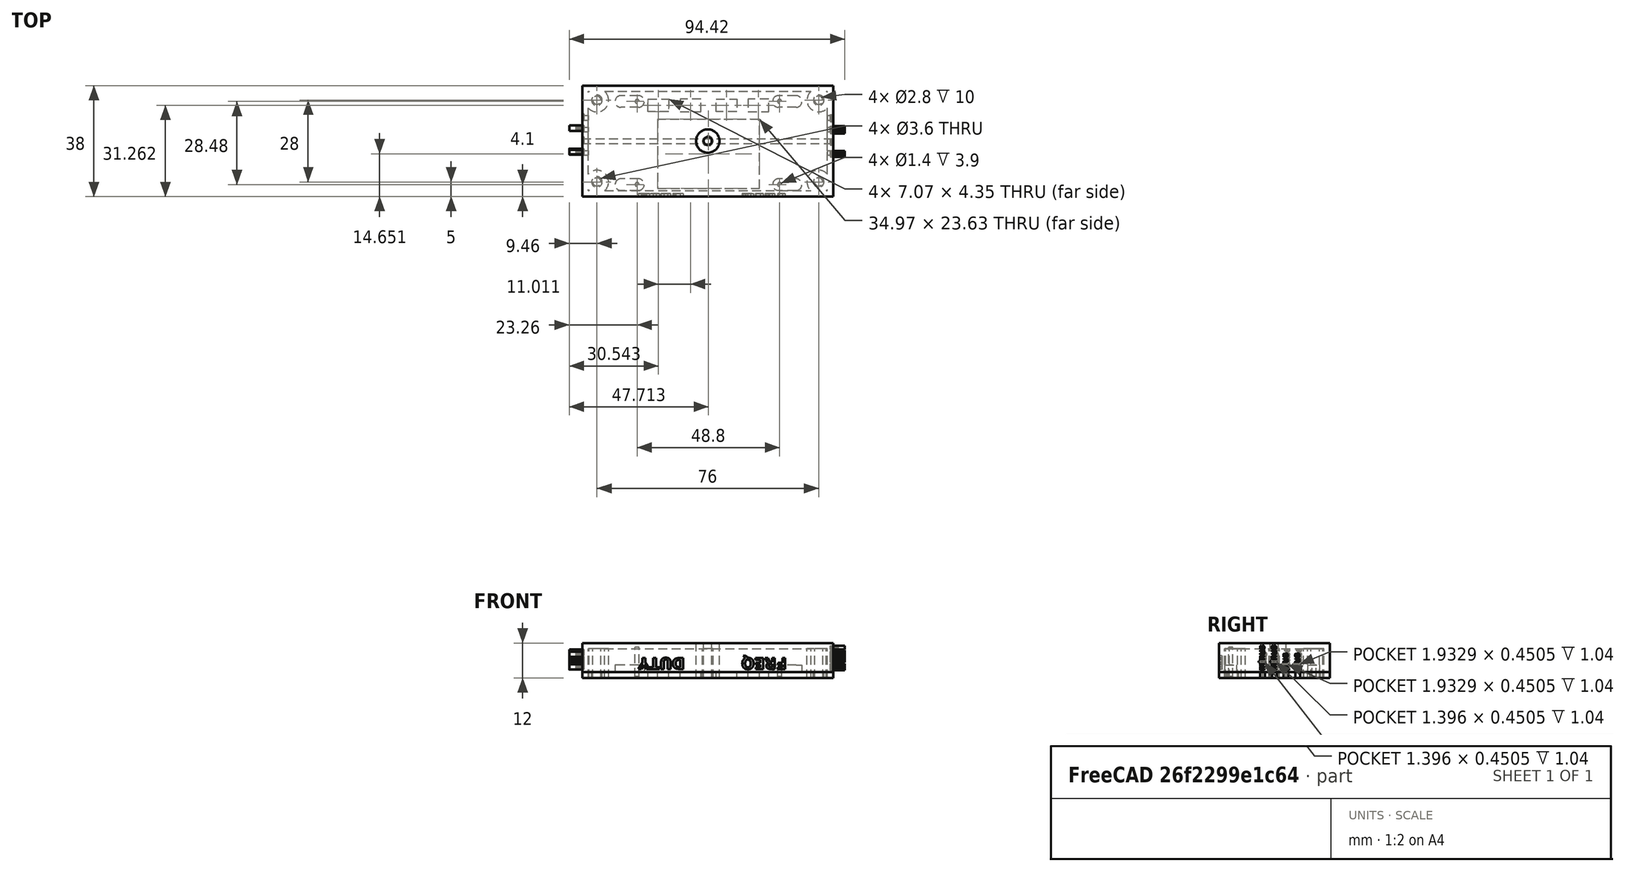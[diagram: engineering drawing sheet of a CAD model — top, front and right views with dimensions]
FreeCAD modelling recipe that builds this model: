
FCSTD DOCUMENT  (FreeCAD 0.19R)
Label: lpwm_v2
License: All rights reserved
LicenseURL: http://en.wikipedia.org/wiki/All_rights_reserved
objects: Part::FeaturePython×10, Part::Part2DObjectPython×7, PartDesign::Body×7, Part::Extrusion×6, PartDesign::FeatureBase×6, Part::Cylinder×4, Part::MultiFuse×4, Part::Cut×3, Part::Box×3, Sketcher::SketchObject×2, PartDesign::Pad×2, App::Part×2, Mesh::Feature×1, Part::Feature×1, Part::Refine×1
note: 48 computed .brp shape members not serialized (recipe doc carries the construction recipe); baked Part::Feature solids carry a one-line shape summary decoded from their .brp

FEATURE [Mesh::Feature] LPWM_pwmGenerator_cover  label="LPWM_pwmGenerator-cover"
FEATURE [Part::Feature] LPWM_pwmGenerator_cover001
  shape: bbox 56.46 x 36.68 x 3.899 mm, 1714 faces, 0 solids (baked)
FEATURE [Part::Refine] LPWM_pwmGenerator_cover001001
  Source = -> LPWM_pwmGenerator_cover001
FEATURE [Part::Part2DObjectPython] Shape2DView  # Draft 2D object (typed FeaturePython)
  Base = -> LPWM_pwmGenerator_cover001001
  FuseArch = false
  HiddenLines = false
  InPlace = true
  Projection = (0.00719287,0.00574245,0.999958)
  ProjectionMode = 0
  SegmentLength = 0.05
  Tessellation = false
  VisibleOnly = false
FEATURE [Sketcher::SketchObject] Sketch  label="top plate sketch"
  ExternalGeometry = -> [Shape2DView]
  FullyConstrained = true
  MapMode = 5
  sketch-geometry (24):
    g0: LineSegment StartX=-20.4532 StartY=14.4374 StartZ=0 EndX=-13.3806 EndY=14.4374 EndZ=0
    g1: LineSegment StartX=-13.3806 StartY=14.4374 StartZ=0 EndX=-13.3806 EndY=10.0869 EndZ=0
    g2: LineSegment StartX=-13.3806 StartY=10.0869 StartZ=0 EndX=-20.4532 EndY=10.0869 EndZ=0
    g3: LineSegment StartX=-20.4532 StartY=10.0869 StartZ=0 EndX=-20.4532 EndY=14.4374 EndZ=0
    g4: LineSegment StartX=-9.44208 StartY=10.0867 StartZ=0 EndX=-2.36949 EndY=10.0867 EndZ=0
    g5: LineSegment StartX=-2.36949 StartY=10.0867 StartZ=0 EndX=-2.36949 EndY=14.4366 EndZ=0
    g6: LineSegment StartX=-2.36949 StartY=14.4366 StartZ=0 EndX=-9.44208 EndY=14.4366 EndZ=0
    g7: LineSegment StartX=-9.44208 StartY=14.4366 StartZ=0 EndX=-9.44208 EndY=10.0867 EndZ=0
    g8: LineSegment StartX=2.84142 StartY=14.4364 StartZ=0 EndX=9.91401 EndY=14.4364 EndZ=0
    g9: LineSegment StartX=9.91401 StartY=14.4364 StartZ=0 EndX=9.91401 EndY=10.0859 EndZ=0
    g10: LineSegment StartX=9.91401 StartY=10.0859 StartZ=0 EndX=2.84142 EndY=10.0859 EndZ=0
    g11: LineSegment StartX=2.84142 StartY=10.0859 StartZ=0 EndX=2.84142 EndY=14.4364 EndZ=0
    g12: LineSegment StartX=13.7837 StartY=10.0858 StartZ=0 EndX=20.8563 EndY=10.0858 EndZ=0
    g13: LineSegment StartX=20.8563 StartY=10.0858 StartZ=0 EndX=20.8563 EndY=14.4357 EndZ=0
    g14: LineSegment StartX=20.8563 StartY=14.4357 StartZ=0 EndX=13.7837 EndY=14.4357 EndZ=0
    g15: LineSegment StartX=13.7837 StartY=14.4357 StartZ=0 EndX=13.7837 EndY=10.0858 EndZ=0
    g16: LineSegment StartX=17.7369 StartY=7.46801 StartZ=0 EndX=-17.2306 EndY=7.46801 EndZ=0
    g17: LineSegment StartX=-17.2306 StartY=7.46801 StartZ=0 EndX=-17.2306 EndY=-16.1666 EndZ=0
    g18: LineSegment StartX=-17.2306 StartY=-16.1666 StartZ=0 EndX=17.7369 EndY=-16.1666 EndZ=0
    g19: LineSegment StartX=17.7369 StartY=-16.1666 StartZ=0 EndX=17.7369 EndY=7.46801 EndZ=0
    g20: LineSegment StartX=-43 StartY=19 StartZ=0 EndX=43 EndY=19 EndZ=0
    g21: LineSegment StartX=43 StartY=19 StartZ=0 EndX=43 EndY=-19 EndZ=0
    g22: LineSegment StartX=43 StartY=-19 StartZ=0 EndX=-43 EndY=-19 EndZ=0
    g23: LineSegment StartX=-43 StartY=-19 StartZ=0 EndX=-43 EndY=19 EndZ=0
  constraints (60):
    c: Coincident(g0,g1)
    c: Coincident(g1,g2)
    c: Coincident(g2,g3)
    c: Coincident(g3,g0)
    c: Horizontal(g0)
    c: Horizontal(g2)
    c: Vertical(g1)
    c: Vertical(g3)
    c: Coincident(g0,g-5)
    c: Coincident(g1,g-6)
    c: Coincident(g4,g5)
    c: Coincident(g5,g6)
    c: Coincident(g6,g7)
    c: Coincident(g7,g4)
    c: Horizontal(g4)
    c: Horizontal(g6)
    c: Vertical(g5)
    c: Vertical(g7)
    c: Coincident(g4,g-7)
    c: Coincident(g5,g-9)
    c: Coincident(g8,g9)
    c: Coincident(g9,g10)
    c: Coincident(g10,g11)
    c: Coincident(g11,g8)
    c: Horizontal(g8)
    c: Horizontal(g10)
    c: Vertical(g9)
    c: Vertical(g11)
    c: Coincident(g8,g-12)
    c: Coincident(g9,g-14)
    c: Coincident(g12,g13)
    c: Coincident(g13,g14)
    c: Coincident(g14,g15)
    c: Coincident(g15,g12)
    c: Horizontal(g12)
    c: Horizontal(g14)
    c: Vertical(g13)
    c: Vertical(g15)
    c: Coincident(g12,g-15)
    c: Coincident(g13,g-17)
    c: Coincident(g16,g17)
    c: Coincident(g17,g18)
    c: Coincident(g18,g19)
    c: Coincident(g19,g16)
    c: Horizontal(g16)
    c: Horizontal(g18)
    c: Vertical(g17)
    c: Vertical(g19)
    c: Coincident(g16,g-22)
    c: Coincident(g17,g-20)
    c: Coincident(g20,g21)
    c: Coincident(g21,g22)
    c: Coincident(g22,g23)
    c: Coincident(g23,g20)
    c: Horizontal(g20)
    c: Vertical(g21)
    c: DistanceX(g20,g20) = 86
    c: Symmetric(g22,g21,g-2)
    c: DistanceY(g23,g23) = 38
    c: Symmetric(g20,g22,g-1)
FEATURE [PartDesign::Pad] Pad  label="top plate body"
  Direction = (1,1,1)
  Length = 2
  Length2 = 100
  Profile = -> Sketch
  Type = 0
FEATURE [Part::Cylinder] Cylinder  label="screw hole"
  Angle = 360
  AttacherType = Attacher::AttachEngine3D
  Height = 10
  Placement = pos=(-24.2,-14.9,0.5) rot=(0,0,1;0rad)
  Radius = 0.7
FEATURE [Part::FeaturePython] Array  label="screw hole array"  # Draft array (typed FeaturePython)
  Angle = 360
  ArrayType = 0
  Axis = (0,0,1)
  Base = -> Cylinder
  Center = (0,0,0)
  Count = 4
  ExpandArray = false
  Fuse = false
  IntervalAxis = (0,0,0)
  IntervalX = (48.8,0,0)
  IntervalY = (0,28.48,0)
  IntervalZ = (0,0,100)
  NumberCircles = 3
  NumberPolar = 5
  NumberX = 2
  NumberY = 2
  NumberZ = 1
  PlacementList = 4 placements: [(-24.2,-14.9,0.5),(-24.2,13.58,0.5),(24.6,-14.9,0.5),(24.6,13.58,0.5)]
  RadialDistance = 50
  ScaleList = (4) [(1,1,1),(1,1,1),(1,1,1),(1,1,1)]
  Symmetry = 1
  TangentialDistance = 25
FEATURE [Sketcher::SketchObject] Sketch001  label="screw hole stand sketch"
  AttachmentOffset = pos=(0,0,2) rot=(0,0,1;0rad)
  ExternalGeometry = -> [Shape2DView]
  FullyConstrained = false
  MapMode = 5
  Placement = pos=(0,0,2) rot=(0,0,1;0rad)
  sketch-geometry (4):
    g0: LineSegment StartX=-23.7668 StartY=-12.9169 StartZ=0 EndX=-29.7668 EndY=-12.9169 EndZ=0
    g1: LineSegment StartX=-23.7668 StartY=-16.9169 StartZ=0 EndX=-29.7668 EndY=-16.9169 EndZ=0
    g2: ArcOfCircle CenterX=-23.7668 CenterY=-14.9169 CenterZ=0 NormalX=0 NormalY=0 NormalZ=1 AngleXU=0 Radius=2 StartAngle=4.71239 EndAngle=7.85398
    g3: ArcOfCircle CenterX=-29.7668 CenterY=-14.9169 CenterZ=0 NormalX=0 NormalY=0 NormalZ=1 AngleXU=0 Radius=2 StartAngle=1.5708 EndAngle=4.71239
  constraints (9):
    c: Horizontal(g0)
    c: Horizontal(g1)
    c: DistanceY(g-3,g1) = 2
    c: DistanceY(g1,g0) = 4
    c: DistanceX(g0,g0) = 6
    c: Tangent(g2,g0) = -1.5708
    c: Tangent(g2,g1) = 1.5708
    c: Tangent(g3,g0) = -1.5708
    c: Tangent(g3,g1) = 1.5708
FEATURE [PartDesign::Pad] Pad001
  Direction = (1,1,1)
  Length = 2.4
  Length2 = 100
  Placement = pos=(0,0,2) rot=(0,0,1;0rad)
  Profile = -> Sketch001
  Type = 0
FEATURE [PartDesign::Body] Body
  Group = -> [Sketch001,Pad001]
  Origin = -> Origin
  Tip = -> Pad001
FEATURE [Part::FeaturePython] Array001  label="screw hole stand array"  # Draft array (typed FeaturePython)
  Angle = 360
  ArrayType = 0
  Axis = (0,0,1)
  Base = -> Body
  Center = (0,0,0)
  Count = 4
  ExpandArray = false
  Fuse = false
  IntervalAxis = (0,0,0)
  IntervalX = (54,0,0)
  IntervalY = (0,28.48,0)
  IntervalZ = (0,0,100)
  NumberCircles = 3
  NumberPolar = 5
  NumberX = 2
  NumberY = 2
  NumberZ = 1
  PlacementList = 4 placements: [(0,0,0),(0,28.48,0),(54,0,0),(54,28.48,0)]
  RadialDistance = 50
  ScaleList = (4) [(1,1,1),(1,1,1),(1,1,1),(1,1,1)]
  Symmetry = 1
  TangentialDistance = 25
FEATURE [Part::MultiFuse] Fusion  label="top plate fusion"
  Shapes = -> [Array001,Pad]
FEATURE [Part::Cylinder] Cylinder001  label="m3 bolt hole"
  Angle = 360
  AttacherType = Attacher::AttachEngine3D
  Height = 10
  Radius = 1.8
FEATURE [Part::FeaturePython] Array002  label="m3 bolt hole array"  # Draft array (typed FeaturePython)
  Angle = 360
  ArrayType = 0
  Axis = (0,0,1)
  Base = -> Cylinder001
  Center = (0,0,0)
  Count = 4
  ExpandArray = false
  Fuse = false
  IntervalAxis = (0,0,0)
  IntervalX = (76,0,0)
  IntervalY = (0,28,0)
  IntervalZ = (0,0,100)
  NumberCircles = 3
  NumberPolar = 5
  NumberX = 2
  NumberY = 2
  NumberZ = 1
  Placement = pos=(-38,-14,-2) rot=(0,0,1;0rad)
  PlacementList = 4 placements: [(0,0,0),(0,28,0),(76,0,0),(76,28,0)]
  RadialDistance = 50
  ScaleList = (4) [(1,1,1),(1,1,1),(1,1,1),(1,1,1)]
  Symmetry = 1
  TangentialDistance = 25
FEATURE [Part::MultiFuse] Fusion001  label="extract fusion"
  Shapes = -> [Array002,Array]
FEATURE [Part::Cut] Cut  label="top plate cut"
  Base = -> Fusion
  Tool = -> Fusion001
FEATURE [App::Part] Part  label="top plate part"
  Group = -> [Cut]
  Origin = -> Origin001
FEATURE [Part::Box] Box  label="bottom outer cube"
  AttacherType = Attacher::AttachEngine3D
  Height = 12
  Length = 86
  Placement = pos=(-43,-19,0) rot=(0,0,1;0rad)
  Width = 38
  expr: .Placement.Base.x = -Length / 2
  expr: .Placement.Base.y = -Width / 2
FEATURE [Part::Box] Box001  label="bottom extract cube"
  AttacherType = Attacher::AttachEngine3D
  Height = 10
  Length = 82
  Placement = pos=(-41,-17,0) rot=(0,0,1;0rad)
  Width = 34
  expr: .Placement.Base.y = -Width / 2
  expr: .Placement.Base.x = -Length / 2
FEATURE [Part::Cylinder] Cylinder002  label="for m3 bolt hole"
  Angle = 360
  AttacherType = Attacher::AttachEngine3D
  Height = 12
  Radius = 1.4
  expr: Height = <<bottom outer cube>>.Height
FEATURE [Part::FeaturePython] Array003  label="for m3 bolt hole array"  # Draft array (typed FeaturePython)
  Angle = 360
  ArrayType = 0
  Axis = (0,0,1)
  Base = -> Cylinder002
  Center = (0,0,0)
  Count = 4
  ExpandArray = false
  Fuse = false
  IntervalAxis = (0,0,0)
  IntervalX = (76,0,0)
  IntervalY = (0,28,0)
  IntervalZ = (0,0,100)
  NumberCircles = 3
  NumberPolar = 5
  NumberX = 2
  NumberY = 2
  NumberZ = 1
  Placement = pos=(-38,-14,-2) rot=(0,0,1;0rad)
  PlacementList = 4 placements: [(0,0,0),(0,28,0),(76,0,0),(76,28,0)]
  RadialDistance = 50
  ScaleList = (4) [(1,1,1),(1,1,1),(1,1,1),(1,1,1)]
  Symmetry = 1
  TangentialDistance = 25
FEATURE [Part::Cylinder] Cylinder003  label="for m3 bolt stand"
  Angle = 360
  AttacherType = Attacher::AttachEngine3D
  Height = 12
  Radius = 4
  expr: Height = <<bottom outer cube>>.Height
FEATURE [Part::FeaturePython] Array004  label="for m3 bolt stand array"  # Draft array (typed FeaturePython)
  Angle = 360
  ArrayType = 0
  Axis = (0,0,1)
  Base = -> Cylinder003
  Center = (0,0,0)
  Count = 4
  ExpandArray = false
  Fuse = false
  IntervalAxis = (0,0,0)
  IntervalX = (76,0,0)
  IntervalY = (0,28,0)
  IntervalZ = (0,0,100)
  NumberCircles = 3
  NumberPolar = 5
  NumberX = 2
  NumberY = 2
  NumberZ = 1
  Placement = pos=(-38,-14,0) rot=(0,0,1;0rad)
  PlacementList = 4 placements: [(0,0,0),(0,28,0),(76,0,0),(76,28,0)]
  RadialDistance = 50
  ScaleList = (4) [(1,1,1),(1,1,1),(1,1,1),(1,1,1)]
  Symmetry = 1
  TangentialDistance = 25
FEATURE [Part::Cut] Cut002  label="bottom cube cut"
  Base = -> Box
  Tool = -> Box001
FEATURE [Part::MultiFuse] Fusion002  label="bottom body fusion"
  Shapes = -> [Array004,Cut002]
FEATURE [Part::Box] Box002  label="wire hole"
  AttacherType = Attacher::AttachEngine3D
  Height = 2
  Length = 86
  Placement = pos=(-43,-0.8,0) rot=(0,0,1;0rad)
  Width = 1.6
  expr: Length = <<bottom outer cube>>.Length
  expr: .Placement.Base.y = -Width / 2
  expr: .Placement.Base.x = -Length / 2
FEATURE [Part::FeaturePython] Array005  label="wire hole array"  # Draft array (typed FeaturePython)
  Angle = 360
  ArrayType = 0
  Axis = (0,0,1)
  Base = -> Box002
  Center = (0,0,0)
  Count = 4
  ExpandArray = false
  Fuse = false
  IntervalAxis = (0,0,0)
  IntervalX = (100,0,0)
  IntervalY = (0,4,0)
  IntervalZ = (0,0,100)
  NumberCircles = 3
  NumberPolar = 5
  NumberX = 1
  NumberY = 4
  NumberZ = 1
  Placement = pos=(0,-4,0) rot=(0,0,1;0rad)
  PlacementList = 4 placements: arithmetic series from (-43,-0.8,0) step (0,4,0) to (-43,11.2,0)
  RadialDistance = 50
  ScaleList = (4) [(1,1,1),(1,1,1),(1,1,1),(1,1,1)]
  Symmetry = 1
  TangentialDistance = 25
  expr: .Placement.Base.y = -.IntervalY.y
FEATURE [Part::Part2DObjectPython] ShapeString  label="PWM ShapeString"  # Draft 2D object (typed FeaturePython)
  FontFile = <path>
  Placement = pos=(-37,-28.06,5.46) rot=(0,0,1;0rad)
  Size = 2
  String = PWM
  Tracking = 0
FEATURE [Part::Extrusion] Extrude
  Base = -> ShapeString
  Dir = (0,0,1)
  DirMode = 2
  FaceMakerClass = Part::FaceMakerBullseye
  LengthFwd = 5
  LengthRev = 0
  Solid = false
  Symmetric = false
FEATURE [PartDesign::FeatureBase] Clone
  BaseFeature = -> Extrude
FEATURE [PartDesign::Body] Body001  label="PWM text body"
  BaseFeature = -> Extrude
  Group = -> [Clone]
  Origin = -> Origin003
  Placement = pos=(-37,31.5,39.8) rot=(0,-1,0;1.5708rad)
  Tip = -> Clone
FEATURE [Part::FeaturePython] Array006  label="PWM text body array"  # Draft array (typed FeaturePython)
  Angle = 360
  ArrayType = 0
  Axis = (0,0,1)
  Base = -> Body001
  Center = (0,0,0)
  Count = 2
  ExpandArray = false
  Fuse = false
  IntervalAxis = (0,0,0)
  IntervalX = (100,0,0)
  IntervalY = (0,4,0)
  IntervalZ = (0,0,100)
  NumberCircles = 3
  NumberPolar = 5
  NumberX = 1
  NumberY = 2
  NumberZ = 1
  PlacementList = 2 placements: [(-37,31.5,39.8),(-37,35.5,39.8)]
  RadialDistance = 50
  ScaleList = (2) [(1,1,1),(1,1,1)]
  Symmetry = 1
  TangentialDistance = 25
FEATURE [Part::Part2DObjectPython] ShapeString001  label="GND ShapeString"  # Draft 2D object (typed FeaturePython)
  FontFile = <path>
  Placement = pos=(-37,-28.06,5.46) rot=(0,0,1;0rad)
  Size = 2
  String = GND
  Tracking = 0
FEATURE [Part::Extrusion] Extrude001
  Base = -> ShapeString001
  Dir = (0,0,1)
  DirMode = 2
  FaceMakerClass = Part::FaceMakerBullseye
  LengthFwd = 5
  LengthRev = 0
  Solid = false
  Symmetric = false
FEATURE [PartDesign::FeatureBase] Clone001
  BaseFeature = -> Extrude001
FEATURE [PartDesign::Body] Body002  label="GND text body"
  Group = -> [Clone001]
  Origin = -> Origin004
  Placement = pos=(-37,23.5,39.8) rot=(0,-1,0;1.5708rad)
  Tip = -> Clone001
FEATURE [Part::FeaturePython] Array007  label="GND text body array"  # Draft array (typed FeaturePython)
  Angle = 360
  ArrayType = 0
  Axis = (0,0,1)
  Base = -> Body002
  Center = (0,0,0)
  Count = 2
  ExpandArray = false
  Fuse = false
  IntervalAxis = (0,0,0)
  IntervalX = (100,0,0)
  IntervalY = (0,4,0)
  IntervalZ = (0,0,100)
  NumberCircles = 3
  NumberPolar = 5
  NumberX = 1
  NumberY = 2
  NumberZ = 1
  PlacementList = 2 placements: [(-37,23.5,39.8),(-37,27.5,39.8)]
  RadialDistance = 50
  ScaleList = (2) [(1,1,1),(1,1,1)]
  Symmetry = 1
  TangentialDistance = 25
FEATURE [Part::Part2DObjectPython] ShapeString002  label="MINUS ShapeString"  # Draft 2D object (typed FeaturePython)
  FontFile = <path>
  Placement = pos=(-37,-28.06,5.46) rot=(0,0,1;0rad)
  Size = 2
  String = minus
  Tracking = 0
FEATURE [Part::Extrusion] Extrude002
  Base = -> ShapeString002
  Dir = (0,0,1)
  DirMode = 2
  FaceMakerClass = Part::FaceMakerBullseye
  LengthFwd = 5
  LengthRev = 0
  Solid = false
  Symmetric = false
FEATURE [PartDesign::FeatureBase] Clone002
  BaseFeature = -> Extrude002
FEATURE [PartDesign::Body] Body003  label="MINUS text body"
  Group = -> [Clone002]
  Origin = -> Origin005
  Placement = pos=(36.5,-31.5,39.5) rot=(0.707107,0,0.707107;3.14159rad)
  Tip = -> Clone002
FEATURE [Part::FeaturePython] Array008  label="MINUS text body array"  # Draft array (typed FeaturePython)
  Angle = 360
  ArrayType = 0
  Axis = (0,0,1)
  Base = -> Body003
  Center = (0,0,0)
  Count = 2
  ExpandArray = false
  Fuse = false
  IntervalAxis = (0,0,0)
  IntervalX = (100,0,0)
  IntervalY = (0,4,0)
  IntervalZ = (0,0,100)
  NumberCircles = 3
  NumberPolar = 5
  NumberX = 1
  NumberY = 2
  NumberZ = 1
  PlacementList = 2 placements: [(36.5,-31.5,39.5),(36.5,-27.5,39.5)]
  RadialDistance = 50
  ScaleList = (2) [(1,1,1),(1,1,1)]
  Symmetry = 1
  TangentialDistance = 25
FEATURE [Part::Part2DObjectPython] ShapeString003  label="PLUS ShapeString001"  # Draft 2D object (typed FeaturePython)
  FontFile = <path>
  Placement = pos=(-37,-28.06,5.46) rot=(0,0,1;0rad)
  Size = 2
  String = plus
  Tracking = 0
FEATURE [Part::Extrusion] Extrude003
  Base = -> ShapeString003
  Dir = (0,0,1)
  DirMode = 2
  FaceMakerClass = Part::FaceMakerBullseye
  LengthFwd = 5
  LengthRev = 0
  Solid = false
  Symmetric = false
FEATURE [PartDesign::FeatureBase] Clone003
  BaseFeature = -> Extrude003
FEATURE [PartDesign::Body] Body004  label="PLUS text body"
  Group = -> [Clone003]
  Origin = -> Origin006
  Placement = pos=(36.5,-23.5,39.5) rot=(0.707107,0,0.707107;3.14159rad)
  Tip = -> Clone003
FEATURE [Part::FeaturePython] Array009  label="PLUS text body array"  # Draft array (typed FeaturePython)
  Angle = 360
  ArrayType = 0
  Axis = (0,0,1)
  Base = -> Body004
  Center = (0,0,0)
  Count = 2
  ExpandArray = false
  Fuse = false
  IntervalAxis = (0,0,0)
  IntervalX = (100,0,0)
  IntervalY = (0,4,0)
  IntervalZ = (0,0,100)
  NumberCircles = 3
  NumberPolar = 5
  NumberX = 1
  NumberY = 2
  NumberZ = 1
  PlacementList = 2 placements: [(36.5,-23.5,39.5),(36.5,-19.5,39.5)]
  RadialDistance = 50
  ScaleList = (2) [(1,1,1),(1,1,1)]
  Symmetry = 1
  TangentialDistance = 25
FEATURE [Part::Part2DObjectPython] ShapeString004  label="FREQ ShapeString"  # Draft 2D object (typed FeaturePython)
  FontFile = <path>
  Placement = pos=(-37,-30.06,4.46) rot=(0,0,1;0rad)
  Size = 4
  String = FREQ
  Tracking = 0
FEATURE [Part::Extrusion] Extrude004
  Base = -> ShapeString004
  Dir = (0,0,1)
  DirMode = 2
  FaceMakerClass = Part::FaceMakerBullseye
  LengthFwd = 5
  LengthRev = 0
  Solid = false
  Symmetric = false
FEATURE [PartDesign::FeatureBase] Clone004
  BaseFeature = -> Extrude004
FEATURE [PartDesign::Body] Body005  label="FREQ text body"
  Group = -> [Clone004]
  Origin = -> Origin007
  Placement = pos=(-10,-13.5,-23.2) rot=(0,0.707107,-0.707107;3.14159rad)
  Tip = -> Clone004
FEATURE [Part::Part2DObjectPython] ShapeString005  label="DUTY ShapeString"  # Draft 2D object (typed FeaturePython)
  FontFile = <path>
  Placement = pos=(-37,-30.06,4.46) rot=(0,0,1;0rad)
  Size = 4
  String = DUTY
  Tracking = 0
FEATURE [Part::Extrusion] Extrude005
  Base = -> ShapeString005
  Dir = (0,0,1)
  DirMode = 2
  FaceMakerClass = Part::FaceMakerBullseye
  LengthFwd = 5
  LengthRev = 0
  Solid = false
  Symmetric = false
FEATURE [PartDesign::FeatureBase] Clone005
  BaseFeature = -> Extrude005
FEATURE [PartDesign::Body] Body006  label="DUTY text body"
  Group = -> [Clone005]
  Origin = -> Origin008
  Placement = pos=(-45,-13.5,-23.2) rot=(0,0.707107,-0.707107;3.14159rad)
  Tip = -> Clone005
FEATURE [Part::MultiFuse] Fusion003  label="bottom hole fusion"
  Shapes = -> [Array003,Array005,Array009,Array008,Array007,Array006,Body005,Body006]
FEATURE [Part::Cut] Cut003  label="bottom cut"
  Base = -> Fusion002
  Tool = -> Fusion003
FEATURE [App::Part] Part001  label="bottom part"
  Group = -> [Cut003]
  Origin = -> Origin002
note: 6 file-system paths scrubbed to <path> (originals preserved in the JSON sidecar)
